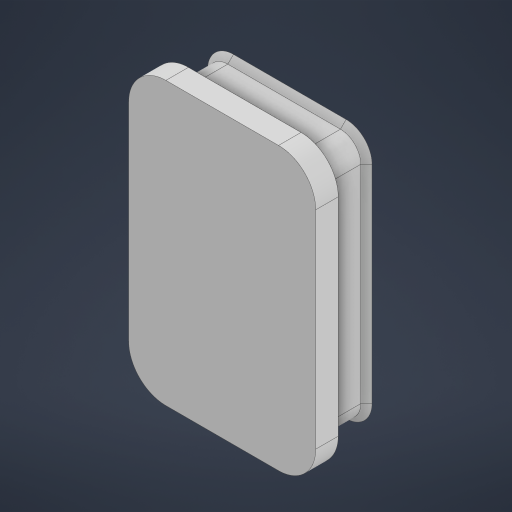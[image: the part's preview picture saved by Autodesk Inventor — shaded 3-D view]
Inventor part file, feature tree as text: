
AUTODESK INVENTOR PART (.ipt)
format: ipt  version: 2023 (Build 270158000, 158)  size: 224,768 bytes
history: native  units: in
note: dims shown in document units (in); Inventor stores cm internally (conversion verified against a paired STEP export)
features: extrude x3, sketch x1, chamfer x1
ambient origin geometry x8: Origin, YZ Plane, XZ Plane, XY Plane, X Axis, Y Axis, Z Axis, Center Point
bodies: Solid1 (feature_tree)
feature tree (5):
  sketch  "Sketch1"  dims[d0=0.2756in d1=0.4409in d2=0.0394in d3=0.0256in d4=0.0394in d5=0.0in d6=0.0039in d7=0.0787in d8=0.0in d9=0.0276in d10=0.0059in d11=0.0689in d12=0.0in d14=0.0098in d15=0.0098in d16=45.0deg]
  extrude  "Extrusion1"  Depth=0.0276in
  extrude  "Extrusion2"  Depth=0.0394in
  extrude  "Extrusion3"  Depth=0.0276in
  chamfer  "Chamfer1"  Distance=0.0394in
